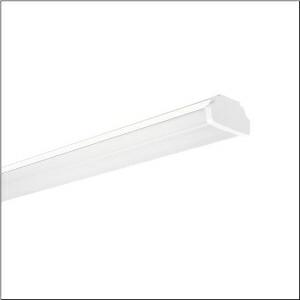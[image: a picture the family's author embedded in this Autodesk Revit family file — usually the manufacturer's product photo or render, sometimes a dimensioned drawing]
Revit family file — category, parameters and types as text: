
# Revit family: modario_r__31_gen_2_53bm812cv685c2_24c7
name_source: partatom
category: Lighting Fixtures
units: mm (PartAtom-declared; Revit-internal decimal feet)

## family parameters
Cut with Voids When Loaded = No
Host = Face
Light Source = No
Part Type = Normal
Room Calculation Point = No
Round Connector Dimension = Use Diameter
Shared = No

## types (1)
- --- (1 x LED, 8970 lm, 49.9 W, 6500K)
    Apparent Load = 50 VA
    CIE Flux Codes = 47 80 95 93 100
    Color Rendering = 80
    Color Temperature = 6500K
    Default Elevation = 1800 mm
    Description = Modario® 31 Gen.2, luminaire insert, of sheet steel, coil coated, white, length: 1.495mm, width: 81mm, height: 82mm, 5x system unit, system units: 299mm, LED rated luminous flux: 8.970lm, light colour: 865, control gear: ON/OFF Multilumen, CLOi, with plug, 3-pole, with phase selection, mains connection: 220..240V, AC, 50/60Hz, start of lifetime: 50W, end of service life: 61W, through-wiring accessed according to module size, primary optical cover: cover, of PMMA, light emission: direct distribution, primary light characteristic: symmetric, protection rating (complete): IP20, protection rating (LED compartment): IP50, insulation class (complete): insulation class I (protective earthing), certification: CE, ENEC, VDE, UKCA, impact resistance: IK03, permissible ambient temperature for indoor applications: -35..+40°C, corresponds to IFS (International Featured Standards) requirements for safety and quality in the food industry, reducing of maximum allowable ambient temperature of 5°C with ceiling mounting, IP40 when using the optional accessory 5TP9018, packaging unit: 1 piece
    Height = 92 mm
    Lamp = 1 x LED
    Lamp Light Flux = 8970 lm
    Lamp Power = 49.9 W
    Lamp count = 1
    Length = 1495 mm
    Luminous efficacy = 180 lm/W
    Manufacturer = Siteco
    ModVariant = No
    Model = 53BM812CV685C2
    Mounting Place = Ceiling
    Mounting Type = Pendant
    Number of Poles = 1
    OnlyDefault = Yes
    Power Factor = 1
    Product Name = Modario® 31 Gen.2
    Product group = luminaire insert
    ProductGroupID = 902
    Protection Class = Protection class I
    Protection Degree = IP 20
    RLX_Detail_Level = 1
    RLX_Emergency_Light_Flux = 0 lm
    RLX_Emergency_Type = 0
    RLX_Emergency_Type_DB = No
    RlxData = <blob elided: 40141 chars, md5=92e4dd77>
    Socket = socket
    Standby Power = 0 W
    System Light Flux = 8970 lm
    System Power = 50 W
    Type Comments = factory setting: luminous flux: 100 % | (A | C | E) | 116 mA
    Type Image = l_1341886.jpg
    URL = http://relux.com
    VarID = @adj_043342
    Voltage = 0 V
    Weight = 0.00 kg
    Width = 81 mm

## geometry (parser evidence)
native form markers: Blend x4, Sweep x12
no freeform markers — native parametric forms only
